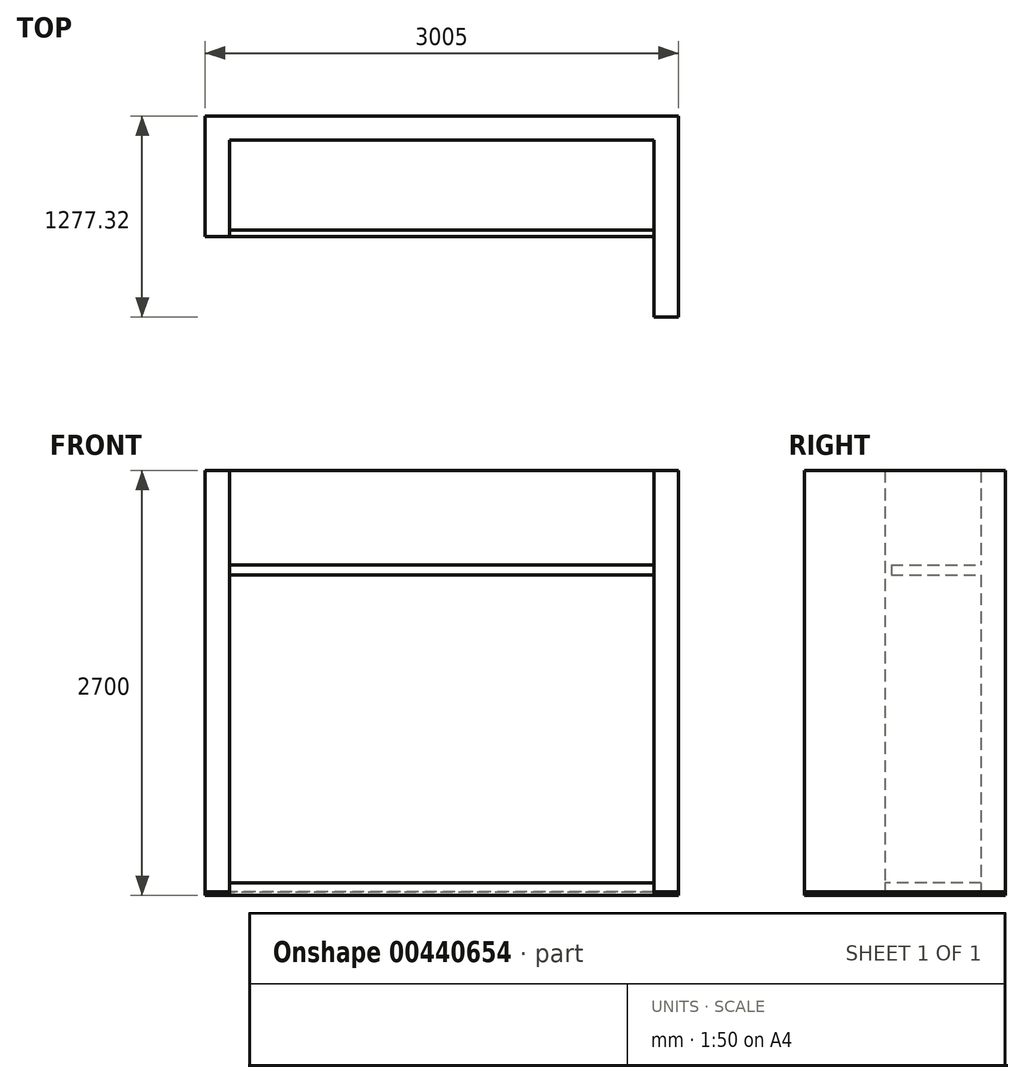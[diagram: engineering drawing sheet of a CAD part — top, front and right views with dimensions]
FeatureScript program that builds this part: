
annotation { "Feature Type Name" : "Feature", "Feature Type Description" : "" }
export const myFeature = defineFeature(function(context is Context, id is Id, definition is map)
    precondition{}
    {
        {
            var Q0;
            Q0=qCreatedBy(makeId("Top.planeOp"),FACE);
            var sketch = newSketch(context, id + "F0", { "sketchPlane" : qUnion([Q0])});
            skLineSegment(sketch, "E0.bottom", {"start": v(-1347.5, 305) * mm, "end": v(1347.5, 305) * mm});
            skLineSegment(sketch, "E0.top", {"start": v(-1347.5, -305) * mm, "end": v(1347.5, -305) * mm});
            skLineSegment(sketch, "E0.left", {"start": v(-1347.5, 305) * mm, "end": v(-1347.5, -305) * mm});
            skLineSegment(sketch, "E0.right", {"start": v(1347.5, 305) * mm, "end": v(1347.5, -305) * mm});
            skPoint(sketch, "E0.middle", {"position": v(0, 0) * mm});
            skSolve(sketch);
        }
        {
            var Q0;
            Q0=qCreatedBy(makeId("Top.planeOp"),FACE);
            var sketch = newSketch(context, id + "F1", { "sketchPlane" : qUnion([Q0])});
            skLineSegment(sketch, "E1", {"start": v(-1347.5, -305) * mm, "end": v(-1502.5, -305) * mm});
            skLineSegment(sketch, "E2", {"start": v(-1502.5, -305) * mm, "end": v(-1502.5, 460) * mm});
            skLineSegment(sketch, "E3", {"start": v(-1502.5, 460) * mm, "end": v(1502.5, 460) * mm});
            skLineSegment(sketch, "E4", {"start": v(1502.5, 460) * mm, "end": v(1502.5, -817.32) * mm});
            skLineSegment(sketch, "E5", {"start": v(1502.5, -817.32) * mm, "end": v(1347.5, -817.32) * mm});
            skLineSegment(sketch, "E6", {"start": v(1347.5, -817.32) * mm, "end": v(1347.5, 305) * mm});
            skLineSegment(sketch, "E7", {"start": v(1347.5, 305) * mm, "end": v(-1347.5, 305) * mm});
            skLineSegment(sketch, "E8", {"start": v(-1347.5, 305) * mm, "end": v(-1347.5, -305) * mm});
            skSolve(sketch);
        }
        {
            var Q0;
            Q0 = qSketchRegion(id + "F1", true);
            extrude(context, id + "F2", {"entities" : qUnion([Q0]), "depth" : 2700 * mm});
        }
        {
            var Q0;
            Q0=makeQuery(id+"F0.imprint","IMPRINT",FACE,{"disambiguationData":[TD([[makeQuery(id+"F0.imprint","IMPRINT",EDGE,{"derivedFrom":sQuery(id+"F0.wireOp",EDGE,"E0.bottom")}),-1.0]])]});
            extrude(context, id + "F3", {"entities" : qUnion([Q0]), "depth" : 80 * mm});
        }
        {
            var Q0;
            Q0 = qSketchRegion(id + "F1", true);
            extrude(context, id + "F4", {"entities" : qUnion([Q0]), "depth" : 25 * mm});
        }
        {
            var Q0;
            Q0=makeQuery(id+"F2.opExtrude","SWEPT_FACE",FACE,{"disambiguationData":[OSD([sQuery(id+"F1.wireOp",EDGE,"E7")])]});
            var sketch = newSketch(context, id + "F5", { "sketchPlane" : qUnion([Q0])});
            skLineSegment(sketch, "E9.bottom", {"start": v(-1347.5, 2100) * mm, "end": v(1347.5, 2100) * mm});
            skLineSegment(sketch, "E9.top", {"start": v(-1347.5, 2035) * mm, "end": v(1347.5, 2035) * mm});
            skLineSegment(sketch, "E9.left", {"start": v(-1347.5, 2100) * mm, "end": v(-1347.5, 2035) * mm});
            skLineSegment(sketch, "E9.right", {"start": v(1347.5, 2100) * mm, "end": v(1347.5, 2035) * mm});
            skSolve(sketch);
        }
        {
            var Q0;
            Q0=makeQuery(id+"F5.imprint","IMPRINT",FACE,{"disambiguationData":[TD([[makeQuery(id+"F5.imprint","IMPRINT",EDGE,{"derivedFrom":sQuery(id+"F5.wireOp",EDGE,"E9.bottom")}),-1.0]])]});
            extrude(context, id + "F6", {"entities" : qUnion([Q0]), "operationType" : NewBodyOperationType.ADD, "depth" : 570 * mm});
        }
    });
